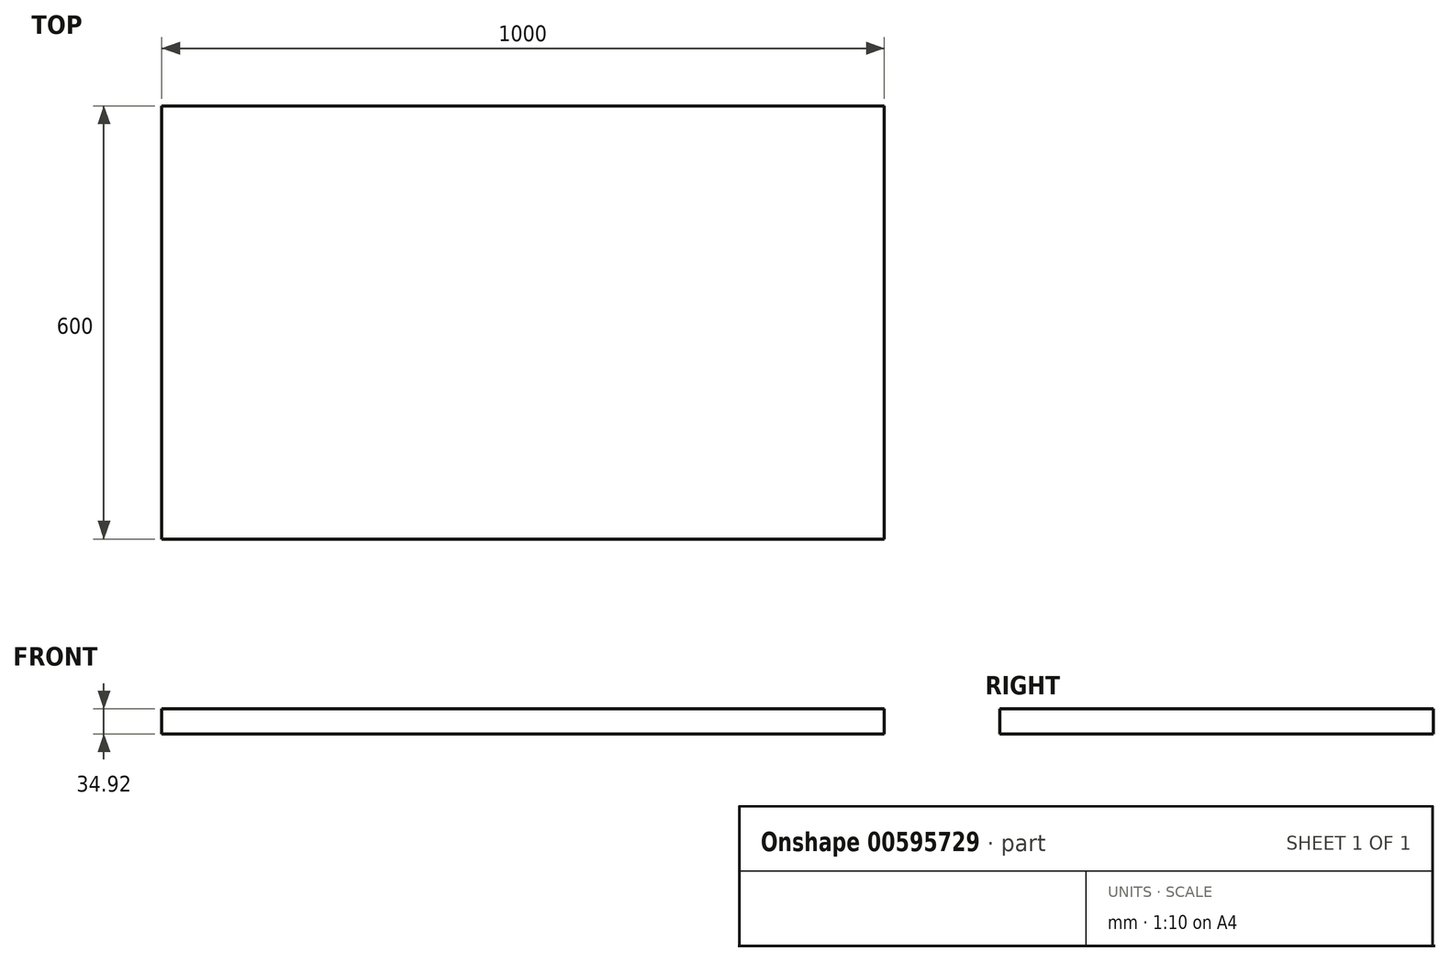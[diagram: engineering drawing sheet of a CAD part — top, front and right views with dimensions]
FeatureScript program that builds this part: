
annotation { "Feature Type Name" : "Feature", "Feature Type Description" : "" }
export const myFeature = defineFeature(function(context is Context, id is Id, definition is map)
    precondition{}
    {
        {
            var Q0;
            Q0=qCreatedBy(makeId("Top.planeOp"),FACE);
            var sketch = newSketch(context, id + "F0", { "sketchPlane" : qUnion([Q0])});
            skLineSegment(sketch, "E0.bottom", {"start": v(500, -300) * mm, "end": v(-500, -300) * mm});
            skLineSegment(sketch, "E0.top", {"start": v(500, 300) * mm, "end": v(-500, 300) * mm});
            skLineSegment(sketch, "E0.left", {"start": v(500, -300) * mm, "end": v(500, 300) * mm});
            skLineSegment(sketch, "E0.right", {"start": v(-500, -300) * mm, "end": v(-500, 300) * mm});
            skPoint(sketch, "E0.middle", {"position": v(0, 0) * mm});
            skSolve(sketch);
        }
        {
            var Q0;
            Q0=makeQuery(id+"F0.imprint","IMPRINT",FACE,{"disambiguationData":[TD([[makeQuery(id+"F0.imprint","IMPRINT",EDGE,{"derivedFrom":sQuery(id+"F0.wireOp",EDGE,"E0.bottom")}),-1.0]])]});
            extrude(context, id + "F1", {"entities" : qUnion([Q0]), "depth" : 34.92 * mm, "offsetDistance" : 25 * mm});
        }
    });
